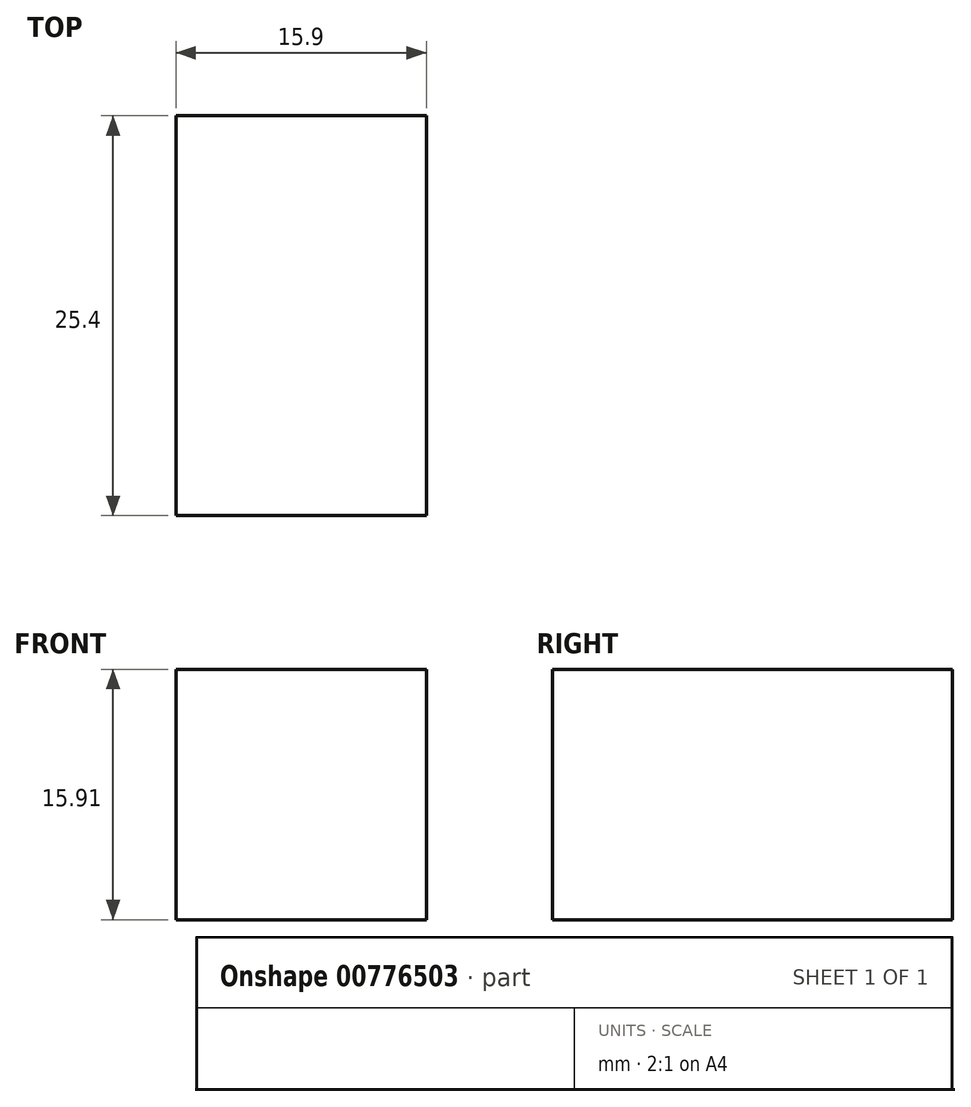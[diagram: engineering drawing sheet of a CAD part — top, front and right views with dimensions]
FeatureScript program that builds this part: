
annotation { "Feature Type Name" : "Feature", "Feature Type Description" : "" }
export const myFeature = defineFeature(function(context is Context, id is Id, definition is map)
    precondition{}
    {
        {
            var Q0;
            Q0=qCreatedBy(makeId("Front.planeOp"),FACE);
            var sketch = newSketch(context, id + "F0", { "sketchPlane" : qUnion([Q0])});
            skLineSegment(sketch, "E0.bottom", {"start": v(10.35, 30.97) * mm, "end": v(26.25, 30.97) * mm});
            skLineSegment(sketch, "E0.top", {"start": v(10.35, 15.06) * mm, "end": v(26.25, 15.06) * mm});
            skLineSegment(sketch, "E0.left", {"start": v(10.35, 30.97) * mm, "end": v(10.35, 15.06) * mm});
            skLineSegment(sketch, "E0.right", {"start": v(26.25, 30.97) * mm, "end": v(26.25, 15.06) * mm});
            skSolve(sketch);
        }
        {
            var Q0;
            Q0 = qSketchRegion(id + "F0", true);
            extrude(context, id + "F1", {"entities" : qUnion([Q0]), "depth" : 4.8 * mm, "offsetDistance" : 25.4 * mm});
        }
        {
            var Q0;
            Q0 = qSketchRegion(id + "F0", true);
            extrude(context, id + "F2", {"entities" : qUnion([Q0]), "operationType" : NewBodyOperationType.ADD, "depth" : 25.4 * mm, "offsetDistance" : 25.4 * mm});
        }
    });
